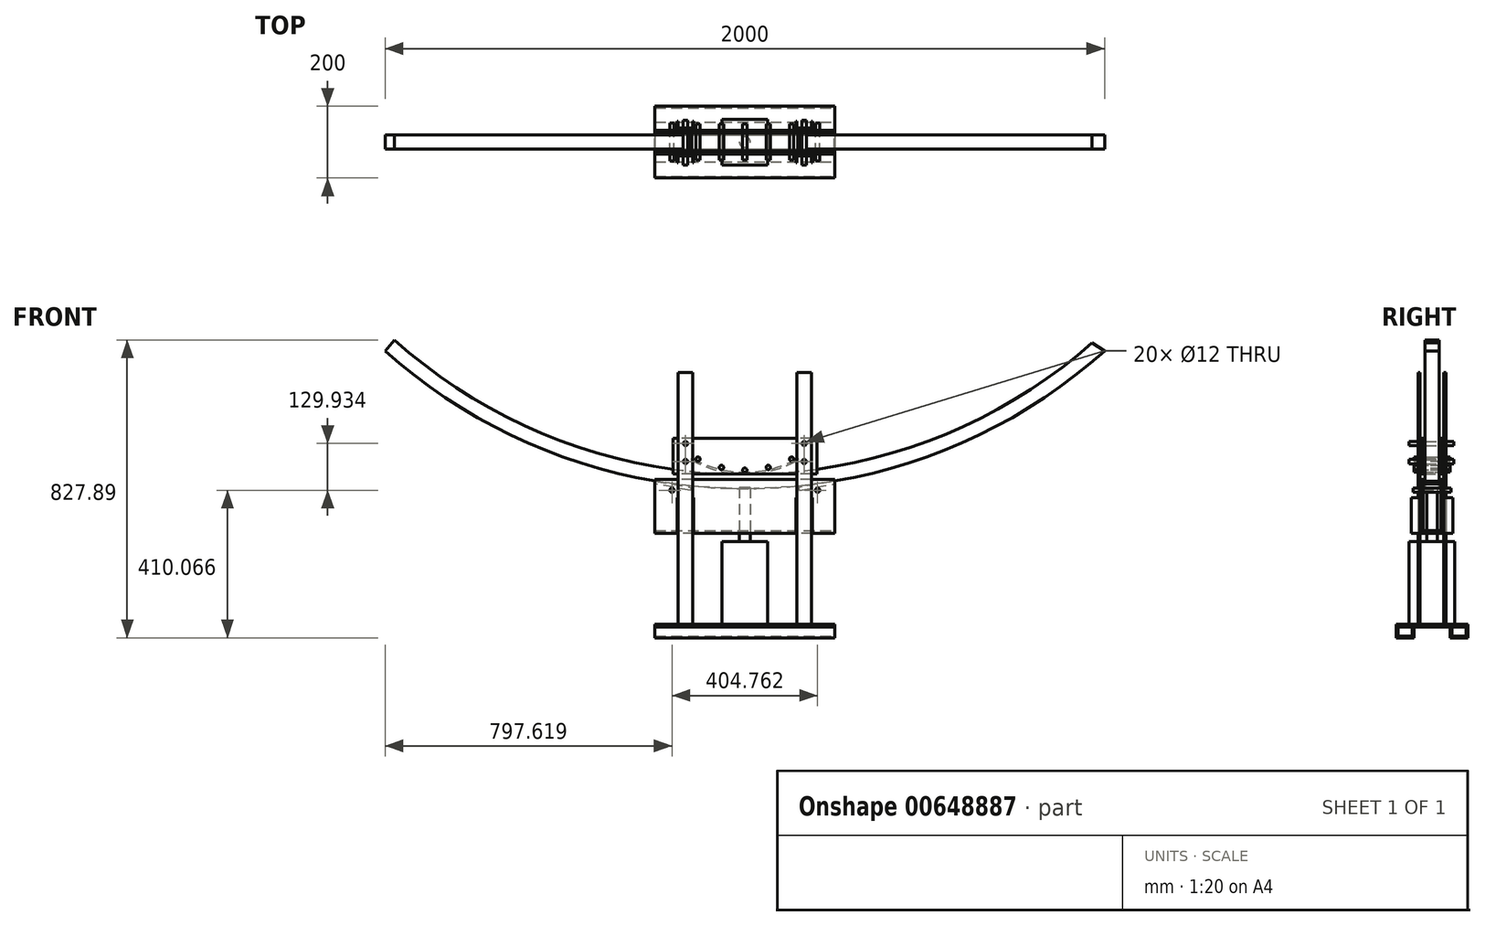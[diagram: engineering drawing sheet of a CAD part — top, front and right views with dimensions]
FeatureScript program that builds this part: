
annotation { "Feature Type Name" : "Feature", "Feature Type Description" : "" }
export const myFeature = defineFeature(function(context is Context, id is Id, definition is map)
    precondition{}
    {
        {
            var Q0;
            Q0=qCreatedBy(makeId("Front.planeOp"),FACE);
            var sketch = newSketch(context, id + "F0", { "sketchPlane" : qUnion([Q0])});
            skArc(sketch, "E0", {"start": v(-1000, 381.97) * mm, "mid": v(0, 0) * mm, "end": v(1000, 381.97) * mm});
            skArc(sketch, "E1", {"start": v(-974.57, 412.89) * mm, "mid": v(-6.16, 40.01) * mm, "end": v(965.36, 404.7) * mm});
            skLineSegment(sketch, "E2", {"start": v(-1000, 381.97) * mm, "end": v(-974.57, 412.89) * mm});
            skLineSegment(sketch, "E3", {"start": v(965.36, 404.7) * mm, "end": v(1000, 381.97) * mm});
            skSolve(sketch);
        }
        {
            var Q0;
            Q0 = qSketchRegion(id + "F0", true);
            extrude(context, id + "F1", {"entities" : qUnion([Q0]), "endBound" : BoundingType.SYMMETRIC, "depth" : 40 * mm, "offsetDistance" : 25 * mm});
        }
        {
            var Q0;
            Q0=qCreatedBy(makeId("Front.planeOp"),FACE);
            var sketch = newSketch(context, id + "F2", { "sketchPlane" : qUnion([Q0])});
            skLineSegment(sketch, "E4", {"start": v(-248.58, 20.64) * mm, "end": v(-150.16, 2.95) * mm});
            skLineSegment(sketch, "E5", {"start": v(-150.16, 2.95) * mm, "end": v(-151.58, -4.92) * mm});
            skLineSegment(sketch, "E6", {"start": v(-151.58, -4.92) * mm, "end": v(-250, 12.77) * mm});
            skLineSegment(sketch, "E7", {"start": v(-250, 12.77) * mm, "end": v(-248.58, 20.64) * mm});
            skLineSegment(sketch, "E8", {"start": v(0, 0) * mm, "end": v(0, 293.06) * mm, "construction": true});
            skLineSegment(sketch, "E9", {"start": v(-364.02, 41.4) * mm, "end": v(0, -24.04) * mm, "construction": true});
            skSolve(sketch);
        }
        {
            var Q0;
            Q0 = qSketchRegion(id + "F2", true);
            extrude(context, id + "F3", {"entities" : qUnion([Q0]), "endBound" : BoundingType.SYMMETRIC, "depth" : 50 * mm, "offsetDistance" : 25 * mm});
        }
        {
            var Q0;
            Q0=makeQuery(id+"F3.opExtrude","SWEPT_BODY",BODY,{"disambiguationData":[OSD([sQuery(id+"F2.wireOp",EDGE,"E4"),sQuery(id+"F2.wireOp",EDGE,"E5"),sQuery(id+"F2.wireOp",EDGE,"E6"),sQuery(id+"F2.wireOp",EDGE,"E7")])]});
            var Q1;
            Q1=makeQuery(id+"F3.opExtrude","SWEPT_BODY",BODY,{"disambiguationData":[OSD([sQuery(id+"F2.wireOp",EDGE,"z8wgNzzR-RekP-I29d-0YfE-zqQQIktSLqPd")])]});
            var Q2;
            Q2=qCreatedBy(makeId("Right.planeOp"),FACE);
            mirror(context, id + "F4", {"entities" : qUnion([Q0, Q1]), "mirrorPlane" : qUnion([Q2])});
        }
        {
            var Q0;
            Q0=qCreatedBy(makeId("Front.planeOp"),FACE);
            var sketch = newSketch(context, id + "F5", { "sketchPlane" : qUnion([Q0])});
            skCircle(sketch, "E10", {"center": v(-202.38, -4.93) * mm, "radius": 6 * mm});
            skLineSegment(sketch, "E11", {"start": v(-200.79, 3.92) * mm, "end": v(-213.25, -65.38) * mm, "construction": true});
            skSolve(sketch);
        }
        {
            var Q0;
            Q0 = qSketchRegion(id + "F5", true);
            extrude(context, id + "F6", {"entities" : qUnion([Q0]), "endBound" : BoundingType.SYMMETRIC, "depth" : (50 + 2 * 8 + 2 * 20) * mm, "offsetDistance" : 25 * mm});
        }
        {
            var Q0;
            Q0=makeQuery(id+"F6.opExtrude","SWEPT_BODY",BODY,{"disambiguationData":[OSD([sQuery(id+"F5.wireOp",EDGE,"E10")])]});
            var Q1;
            Q1=qCreatedBy(makeId("Right.planeOp"),FACE);
            mirror(context, id + "F7", {"entities" : qUnion([Q0]), "mirrorPlane" : qUnion([Q1])});
        }
        {
            var Q0;
            Q0=qCreatedBy(makeId("Front.planeOp"),FACE);
            cPlane(context, id + "F8", {"entities" : qUnion([Q0]), "cplaneType" : CPlaneType.OFFSET, "offset" : 25 * mm, "width" : 150 * mm, "height" : 150 * mm});
        }
        {
            var Q0;
            Q0=qCreatedBy(id+"F8.planeOp",FACE);
            var sketch = newSketch(context, id + "F9", { "sketchPlane" : qUnion([Q0])});
            skLineSegment(sketch, "E12.bottom", {"start": v(250, -125) * mm, "end": v(-250, -125) * mm});
            skLineSegment(sketch, "E12.top", {"start": v(250, 25) * mm, "end": v(-250, 25) * mm});
            skLineSegment(sketch, "E12.left", {"start": v(250, -125) * mm, "end": v(250, 25) * mm});
            skLineSegment(sketch, "E12.right", {"start": v(-250, -125) * mm, "end": v(-250, 25) * mm});
            skPoint(sketch, "E12.middle", {"position": v(0, -50) * mm});
            skSolve(sketch);
        }
        {
            var Q0;
            Q0 = qSketchRegion(id + "F9", true);
            extrude(context, id + "F10", {"entities" : qUnion([Q0]), "depth" : 8 * mm, "offsetDistance" : 25 * mm});
        }
        {
            var Q0;
            Q0=makeQuery(id+"F6.opExtrude","SWEPT_BODY",BODY,{"disambiguationData":[OSD([sQuery(id+"F5.wireOp",EDGE,"E10")])]});
            var Q1;
            Q1=makeQuery(id+"F7.opPattern","COPY",BODY,{"derivedFrom":makeQuery(id+"F6.opExtrude","SWEPT_BODY",BODY,{"disambiguationData":[OSD([sQuery(id+"F5.wireOp",EDGE,"E10")])]}),"instanceName":"1"});
            var Q2;
            Q2=makeQuery(id+"F10.opExtrude","SWEPT_BODY",BODY,{"disambiguationData":[OSD([sQuery(id+"F9.wireOp",EDGE,"E12.bottom"),sQuery(id+"F9.wireOp",EDGE,"E12.top"),sQuery(id+"F9.wireOp",EDGE,"E12.left"),sQuery(id+"F9.wireOp",EDGE,"E12.right")])]});
            booleanBodies(context, id + "F11", {"operationType" : BooleanOperationType.SUBTRACTION, "tools" : qUnion([Q0, Q1]), "targets" : qUnion([Q2]), "keepTools" : true});
        }
        {
            var Q0;
            Q0=makeQuery(id+"F10.opExtrude","SWEPT_BODY",BODY,{"disambiguationData":[OSD([sQuery(id+"F9.wireOp",EDGE,"E12.bottom"),sQuery(id+"F9.wireOp",EDGE,"E12.top"),sQuery(id+"F9.wireOp",EDGE,"E12.left"),sQuery(id+"F9.wireOp",EDGE,"E12.right")])]});
            var Q1;
            Q1=qCreatedBy(makeId("Front.planeOp"),FACE);
            mirror(context, id + "F12", {"entities" : qUnion([Q0]), "mirrorPlane" : qUnion([Q1])});
        }
        {
            var Q0;
            Q0=qCreatedBy(id+"F8.planeOp",FACE);
            var sketch = newSketch(context, id + "F13", { "sketchPlane" : qUnion([Q0])});
            skLineSegment(sketch, "E13.bottom", {"start": v(200, 40) * mm, "end": v(-200, 40) * mm});
            skLineSegment(sketch, "E13.top", {"start": v(200, 140) * mm, "end": v(-200, 140) * mm});
            skLineSegment(sketch, "E13.left", {"start": v(200, 40) * mm, "end": v(200, 140) * mm});
            skLineSegment(sketch, "E13.right", {"start": v(-200, 40) * mm, "end": v(-200, 140) * mm});
            skPoint(sketch, "E13.middle", {"position": v(0, 90) * mm});
            skSolve(sketch);
        }
        {
            var Q0;
            Q0 = qSketchRegion(id + "F13", true);
            extrude(context, id + "F14", {"entities" : qUnion([Q0]), "depth" : 8 * mm, "offsetDistance" : 25 * mm});
        }
        {
            var Q0;
            Q0=makeQuery(id+"F14.opExtrude","SWEPT_BODY",BODY,{"disambiguationData":[OSD([sQuery(id+"F13.wireOp",EDGE,"E13.bottom"),sQuery(id+"F13.wireOp",EDGE,"E13.top"),sQuery(id+"F13.wireOp",EDGE,"E13.left"),sQuery(id+"F13.wireOp",EDGE,"E13.right")])]});
            var Q1;
            Q1=qCreatedBy(makeId("Front.planeOp"),FACE);
            mirror(context, id + "F15", {"entities" : qUnion([Q0]), "mirrorPlane" : qUnion([Q1])});
        }
        {
            var Q0;
            Q0=makeQuery(id+"F12.opPattern","COPY",FACE,{"derivedFrom":makeQuery(id+"F10.opExtrude","SWEPT_FACE",FACE,{"disambiguationData":[OSD([sQuery(id+"F9.wireOp",EDGE,"E12.bottom")])]}),"instanceName":"1"});
            var sketch = newSketch(context, id + "F16", { "sketchPlane" : qUnion([Q0])});
            skLineSegment(sketch, "E14.bottom", {"start": v(-25, 25) * mm, "end": v(250, 25) * mm});
            skLineSegment(sketch, "E14.top", {"start": v(-25, -25) * mm, "end": v(250, -25) * mm});
            skLineSegment(sketch, "E14.right", {"start": v(250, 25) * mm, "end": v(250, -25) * mm});
            skPoint(sketch, "E14.middle", {"position": v(112.5, 0) * mm});
            skLineSegment(sketch, "E15.bottom", {"start": v(-250, 25) * mm, "end": v(25, 25) * mm});
            skLineSegment(sketch, "E15.top", {"start": v(-250, -25) * mm, "end": v(25, -25) * mm});
            skLineSegment(sketch, "E15.left", {"start": v(-250, 25) * mm, "end": v(-250, -25) * mm});
            skPoint(sketch, "E15.middle", {"position": v(-112.5, 0) * mm});
            skSolve(sketch);
        }
        {
            var Q0;
            Q0 = qSketchRegion(id + "F16", true);
            extrude(context, id + "F17", {"entities" : qUnion([Q0]), "oppositeDirection" : true, "depth" : 8 * mm, "offsetDistance" : 25 * mm});
        }
        {
            var Q0;
            Q0=qCreatedBy(makeId("Front.planeOp"),FACE);
            var sketch = newSketch(context, id + "F18", { "sketchPlane" : qUnion([Q0])});
            skArc(sketch, "E16", {"start": v(150, 80.2) * mm, "mid": v(0, 40) * mm, "end": v(-150, 80.2) * mm});
            skLineSegment(sketch, "E17", {"start": v(180.7, 40) * mm, "end": v(-137.19, 40) * mm, "construction": true});
            skArc(sketch, "E18", {"start": v(147.5, 84.52) * mm, "mid": v(0, 45) * mm, "end": v(-147.5, 84.52) * mm});
            skLineSegment(sketch, "E19", {"start": v(150, 80.2) * mm, "end": v(147.5, 84.52) * mm});
            skLineSegment(sketch, "E20", {"start": v(-147.5, 84.52) * mm, "end": v(-150, 80.2) * mm});
            skLineSegment(sketch, "E21", {"start": v(-150, 80.2) * mm, "end": v(-137.46, 72.95) * mm, "construction": true});
            skLineSegment(sketch, "E22", {"start": v(192.57, 104.77) * mm, "end": v(150, 80.2) * mm, "construction": true});
            skSolve(sketch);
        }
        {
            var Q0;
            Q0 = qSketchRegion(id + "F18", true);
            extrude(context, id + "F19", {"entities" : qUnion([Q0]), "endBound" : BoundingType.SYMMETRIC, "depth" : 50 * mm, "offsetDistance" : 25 * mm});
        }
        {
            var Q0;
            Q0=qCreatedBy(makeId("Front.planeOp"),FACE);
            var sketch = newSketch(context, id + "F20", { "sketchPlane" : qUnion([Q0])});
            skCircle(sketch, "E23", {"center": v(0, 51) * mm, "radius": 6 * mm});
            skCircle(sketch, "E24", {"center": v(-65, 58.4) * mm, "radius": 6 * mm});
            skCircle(sketch, "E25", {"center": v(65, 58.4) * mm, "radius": 6 * mm});
            skCircle(sketch, "E26", {"center": v(-130, 81.89) * mm, "radius": 6 * mm});
            skCircle(sketch, "E27", {"center": v(130, 81.89) * mm, "radius": 6 * mm});
            skLineSegment(sketch, "E28", {"start": v(0, 0) * mm, "end": v(0, 155.47) * mm, "construction": true});
            skSolve(sketch);
        }
        {
            var Q0;
            Q0 = qSketchRegion(id + "F20", true);
            extrude(context, id + "F21", {"entities" : qUnion([Q0]), "endBound" : BoundingType.SYMMETRIC, "depth" : 100 * mm, "offsetDistance" : 25 * mm});
        }
        {
            var Q0;
            Q0=qCreatedBy(makeId("Top.planeOp"),FACE);
            cPlane(context, id + "F22", {"entities" : qUnion([Q0]), "cplaneType" : CPlaneType.OFFSET, "offset" : (250 + 127) * mm, "oppositeDirection" : true, "width" : 150 * mm, "height" : 150 * mm});
        }
        {
            var Q0;
            Q0=qCreatedBy(id+"F22.planeOp",FACE);
            var sketch = newSketch(context, id + "F23", { "sketchPlane" : qUnion([Q0])});
            skLineSegment(sketch, "E29.bottom", {"start": v(63.5, 63.5) * mm, "end": v(-63.5, 63.5) * mm});
            skLineSegment(sketch, "E29.top", {"start": v(63.5, -63.5) * mm, "end": v(-63.5, -63.5) * mm});
            skLineSegment(sketch, "E29.left", {"start": v(63.5, 63.5) * mm, "end": v(63.5, -63.5) * mm});
            skLineSegment(sketch, "E29.right", {"start": v(-63.5, 63.5) * mm, "end": v(-63.5, -63.5) * mm});
            skPoint(sketch, "E29.middle", {"position": v(0, 0) * mm});
            skSolve(sketch);
        }
        {
            var Q0;
            Q0 = qSketchRegion(id + "F23", true);
            extrude(context, id + "F24", {"entities" : qUnion([Q0]), "depth" : 230 * mm, "offsetDistance" : 25 * mm});
        }
        {
            var Q0;
            Q0=makeQuery(id+"F24.opExtrude","CAP_FACE",FACE,{"disambiguationData":[OSD([sQuery(id+"F23.wireOp",EDGE,"E29.bottom"),sQuery(id+"F23.wireOp",EDGE,"E29.top"),sQuery(id+"F23.wireOp",EDGE,"E29.left"),sQuery(id+"F23.wireOp",EDGE,"E29.right")])],"isStart":false});
            var sketch = newSketch(context, id + "F25", { "sketchPlane" : qUnion([Q0])});
            skCircle(sketch, "E30", {"center": v(0, 0) * mm, "radius": 15 * mm});
            skSolve(sketch);
        }
        {
            var Q0;
            Q0 = qSketchRegion(id + "F25", true);
            extrude(context, id + "F26", {"entities" : qUnion([Q0]), "depth" : 150 * mm, "offsetDistance" : 25 * mm});
        }
        {
            var Q0;
            Q0=qCreatedBy(id+"F22.planeOp",FACE);
            var sketch = newSketch(context, id + "F27", { "sketchPlane" : qUnion([Q0])});
            skLineSegment(sketch, "E31.bottom", {"start": v(250, 100) * mm, "end": v(-250, 100) * mm});
            skLineSegment(sketch, "E31.top", {"start": v(250, -100) * mm, "end": v(-250, -100) * mm});
            skLineSegment(sketch, "E31.left", {"start": v(250, 100) * mm, "end": v(250, -100) * mm});
            skLineSegment(sketch, "E31.right", {"start": v(-250, 100) * mm, "end": v(-250, -100) * mm});
            skPoint(sketch, "E31.middle", {"position": v(0, 0) * mm});
            skSolve(sketch);
        }
        {
            var Q0;
            Q0 = qSketchRegion(id + "F27", true);
            extrude(context, id + "F28", {"entities" : qUnion([Q0]), "oppositeDirection" : true, "depth" : 8 * mm, "offsetDistance" : 25 * mm});
        }
        {
            var Q0;
            Q0=makeQuery(id+"F28.opExtrude","CAP_FACE",FACE,{"disambiguationData":[OSD([sQuery(id+"F27.wireOp",EDGE,"E31.bottom"),sQuery(id+"F27.wireOp",EDGE,"E31.top"),sQuery(id+"F27.wireOp",EDGE,"E31.left"),sQuery(id+"F27.wireOp",EDGE,"E31.right")])],"isStart":true});
            var sketch = newSketch(context, id + "F29", { "sketchPlane" : qUnion([Q0])});
            skLineSegment(sketch, "E32.bottom", {"start": v(-185, 39) * mm, "end": v(-145, 39) * mm});
            skLineSegment(sketch, "E32.top", {"start": v(-185, 33) * mm, "end": v(-145, 33) * mm});
            skLineSegment(sketch, "E32.left", {"start": v(-185, 39) * mm, "end": v(-185, 33) * mm});
            skLineSegment(sketch, "E32.right", {"start": v(-145, 39) * mm, "end": v(-145, 33) * mm});
            skLineSegment(sketch, "E33.bottom", {"start": v(-185, -33) * mm, "end": v(-145, -33) * mm});
            skLineSegment(sketch, "E33.top", {"start": v(-185, -39) * mm, "end": v(-145, -39) * mm});
            skLineSegment(sketch, "E33.left", {"start": v(-185, -33) * mm, "end": v(-185, -39) * mm});
            skLineSegment(sketch, "E33.right", {"start": v(-145, -33) * mm, "end": v(-145, -39) * mm});
            skLineSegment(sketch, "E34.bottom", {"start": v(145, -33) * mm, "end": v(185, -33) * mm});
            skLineSegment(sketch, "E34.top", {"start": v(145, -39) * mm, "end": v(185, -39) * mm});
            skLineSegment(sketch, "E34.left", {"start": v(145, -33) * mm, "end": v(145, -39) * mm});
            skLineSegment(sketch, "E34.right", {"start": v(185, -33) * mm, "end": v(185, -39) * mm});
            skLineSegment(sketch, "E35.bottom", {"start": v(145, 39) * mm, "end": v(185, 39) * mm});
            skLineSegment(sketch, "E35.top", {"start": v(145, 33) * mm, "end": v(185, 33) * mm});
            skLineSegment(sketch, "E35.left", {"start": v(145, 39) * mm, "end": v(145, 33) * mm});
            skLineSegment(sketch, "E35.right", {"start": v(185, 39) * mm, "end": v(185, 33) * mm});
            skSolve(sketch);
        }
        {
            var Q0;
            Q0 = qSketchRegion(id + "F29", true);
            extrude(context, id + "F30", {"entities" : qUnion([Q0]), "depth" : 700 * mm, "offsetDistance" : 25 * mm});
        }
        {
            var Q0;
            Q0=makeQuery(id+"F30.opExtrude","SWEPT_FACE",FACE,{"disambiguationData":[OSD([sQuery(id+"F29.wireOp",EDGE,"E33.top")])]});
            var sketch = newSketch(context, id + "F31", { "sketchPlane" : qUnion([Q0])});
            skCircle(sketch, "E36", {"center": v(-165, 125) * mm, "radius": 6 * mm});
            skCircle(sketch, "E37", {"center": v(-165, 75) * mm, "radius": 6 * mm});
            skCircle(sketch, "E38", {"center": v(165, 125) * mm, "radius": 6 * mm});
            skCircle(sketch, "E39", {"center": v(165, 75) * mm, "radius": 6 * mm});
            skLineSegment(sketch, "E40", {"start": v(-165, 125) * mm, "end": v(-165, 75) * mm, "construction": true});
            skLineSegment(sketch, "E41", {"start": v(165, 125) * mm, "end": v(165, 75) * mm, "construction": true});
            skSolve(sketch);
        }
        {
            var Q0;
            Q0 = qSketchRegion(id + "F31", true);
            extrude(context, id + "F32", {"entities" : qUnion([Q0]), "depth" : 25 * mm, "offsetDistance" : 25 * mm, "hasSecondDirection" : true, "secondDirectionOppositeDirection" : true, "secondDirectionDepth" : 100 * mm});
        }
        {
            var Q0;
            Q0=makeQuery(id+"F32.opExtrude","SWEPT_BODY",BODY,{"disambiguationData":[OSD([sQuery(id+"F31.wireOp",EDGE,"E37")])]});
            var Q1;
            Q1=makeQuery(id+"F32.opExtrude","SWEPT_BODY",BODY,{"disambiguationData":[OSD([sQuery(id+"F31.wireOp",EDGE,"E39")])]});
            var Q2;
            Q2=makeQuery(id+"F32.opExtrude","SWEPT_BODY",BODY,{"disambiguationData":[OSD([sQuery(id+"F31.wireOp",EDGE,"E38")])]});
            var Q3;
            Q3=makeQuery(id+"F32.opExtrude","SWEPT_BODY",BODY,{"disambiguationData":[OSD([sQuery(id+"F31.wireOp",EDGE,"E36")])]});
            var Q4;
            Q4=makeQuery(id+"F30.opExtrude","SWEPT_BODY",BODY,{"disambiguationData":[OSD([sQuery(id+"F29.wireOp",EDGE,"E33.bottom"),sQuery(id+"F29.wireOp",EDGE,"E33.top"),sQuery(id+"F29.wireOp",EDGE,"E33.left"),sQuery(id+"F29.wireOp",EDGE,"E33.right")])]});
            var Q5;
            Q5=makeQuery(id+"F30.opExtrude","SWEPT_BODY",BODY,{"disambiguationData":[OSD([sQuery(id+"F29.wireOp",EDGE,"E32.bottom"),sQuery(id+"F29.wireOp",EDGE,"E32.top"),sQuery(id+"F29.wireOp",EDGE,"E32.left"),sQuery(id+"F29.wireOp",EDGE,"E32.right")])]});
            var Q6;
            Q6=makeQuery(id+"F14.opExtrude","SWEPT_BODY",BODY,{"disambiguationData":[OSD([sQuery(id+"F13.wireOp",EDGE,"E13.bottom"),sQuery(id+"F13.wireOp",EDGE,"E13.top"),sQuery(id+"F13.wireOp",EDGE,"E13.left"),sQuery(id+"F13.wireOp",EDGE,"E13.right")])]});
            var Q7;
            Q7=makeQuery(id+"F15.opPattern","COPY",BODY,{"derivedFrom":makeQuery(id+"F14.opExtrude","SWEPT_BODY",BODY,{"disambiguationData":[OSD([sQuery(id+"F13.wireOp",EDGE,"E13.bottom"),sQuery(id+"F13.wireOp",EDGE,"E13.top"),sQuery(id+"F13.wireOp",EDGE,"E13.left"),sQuery(id+"F13.wireOp",EDGE,"E13.right")])]}),"instanceName":"1"});
            var Q8;
            Q8=makeQuery(id+"F30.opExtrude","SWEPT_BODY",BODY,{"disambiguationData":[OSD([sQuery(id+"F29.wireOp",EDGE,"E35.bottom"),sQuery(id+"F29.wireOp",EDGE,"E35.top"),sQuery(id+"F29.wireOp",EDGE,"E35.left"),sQuery(id+"F29.wireOp",EDGE,"E35.right")])]});
            var Q9;
            Q9=makeQuery(id+"F30.opExtrude","SWEPT_BODY",BODY,{"disambiguationData":[OSD([sQuery(id+"F29.wireOp",EDGE,"E34.bottom"),sQuery(id+"F29.wireOp",EDGE,"E34.top"),sQuery(id+"F29.wireOp",EDGE,"E34.left"),sQuery(id+"F29.wireOp",EDGE,"E34.right")])]});
            booleanBodies(context, id + "F33", {"operationType" : BooleanOperationType.SUBTRACTION, "tools" : qUnion([Q0, Q1, Q2, Q3]), "targets" : qUnion([Q4, Q5, Q6, Q7, Q8, Q9]), "keepTools" : true});
        }
        {
            var Q0;
            Q0=makeQuery(id+"F10.opExtrude","SWEPT_FACE",FACE,{"disambiguationData":[OSD([sQuery(id+"F9.wireOp",EDGE,"E12.bottom")])]});
            var sketch = newSketch(context, id + "F34", { "sketchPlane" : qUnion([Q0])});
            skLineSegment(sketch, "E42.bottom", {"start": v(-185, 33) * mm, "end": v(-188, 33) * mm});
            skLineSegment(sketch, "E42.top", {"start": v(-185, 58) * mm, "end": v(-188, 58) * mm});
            skLineSegment(sketch, "E42.left", {"start": v(-185, 33) * mm, "end": v(-185, 58) * mm});
            skLineSegment(sketch, "E42.right", {"start": v(-188, 33) * mm, "end": v(-188, 58) * mm});
            skLineSegment(sketch, "E43.bottom", {"start": v(-145, 58) * mm, "end": v(-142, 58) * mm});
            skLineSegment(sketch, "E43.top", {"start": v(-145, 33) * mm, "end": v(-142, 33) * mm});
            skLineSegment(sketch, "E43.left", {"start": v(-145, 58) * mm, "end": v(-145, 33) * mm});
            skLineSegment(sketch, "E43.right", {"start": v(-142, 58) * mm, "end": v(-142, 33) * mm});
            skSolve(sketch);
        }
        {
            var Q0;
            Q0 = qSketchRegion(id + "F34", true);
            extrude(context, id + "F35", {"entities" : qUnion([Q0]), "oppositeDirection" : true, "depth" : 100 * mm, "offsetDistance" : 25 * mm});
        }
        {
            var Q0;
            Q0=makeQuery(id+"F35.opExtrude","SWEPT_BODY",BODY,{"disambiguationData":[OSD([sQuery(id+"F34.wireOp",EDGE,"E42.bottom"),sQuery(id+"F34.wireOp",EDGE,"E42.top"),sQuery(id+"F34.wireOp",EDGE,"E42.left"),sQuery(id+"F34.wireOp",EDGE,"E42.right")])]});
            var Q1;
            Q1=makeQuery(id+"F35.opExtrude","SWEPT_BODY",BODY,{"disambiguationData":[OSD([sQuery(id+"F34.wireOp",EDGE,"E43.bottom"),sQuery(id+"F34.wireOp",EDGE,"E43.top"),sQuery(id+"F34.wireOp",EDGE,"E43.left"),sQuery(id+"F34.wireOp",EDGE,"E43.right")])]});
            var Q2;
            Q2=qCreatedBy(makeId("Right.planeOp"),FACE);
            mirror(context, id + "F36", {"entities" : qUnion([Q0, Q1]), "mirrorPlane" : qUnion([Q2])});
        }
        {
            var Q0;
            Q0=makeQuery(id+"F35.opExtrude","SWEPT_BODY",BODY,{"disambiguationData":[OSD([sQuery(id+"F34.wireOp",EDGE,"E42.bottom"),sQuery(id+"F34.wireOp",EDGE,"E42.top"),sQuery(id+"F34.wireOp",EDGE,"E42.left"),sQuery(id+"F34.wireOp",EDGE,"E42.right")])]});
            var Q1;
            Q1=makeQuery(id+"F35.opExtrude","SWEPT_BODY",BODY,{"disambiguationData":[OSD([sQuery(id+"F34.wireOp",EDGE,"E43.bottom"),sQuery(id+"F34.wireOp",EDGE,"E43.top"),sQuery(id+"F34.wireOp",EDGE,"E43.left"),sQuery(id+"F34.wireOp",EDGE,"E43.right")])]});
            var Q2;
            Q2=makeQuery(id+"F36.opPattern","COPY",BODY,{"derivedFrom":makeQuery(id+"F35.opExtrude","SWEPT_BODY",BODY,{"disambiguationData":[OSD([sQuery(id+"F34.wireOp",EDGE,"E43.bottom"),sQuery(id+"F34.wireOp",EDGE,"E43.top"),sQuery(id+"F34.wireOp",EDGE,"E43.left"),sQuery(id+"F34.wireOp",EDGE,"E43.right")])]}),"instanceName":"1"});
            var Q3;
            Q3=makeQuery(id+"F36.opPattern","COPY",BODY,{"derivedFrom":makeQuery(id+"F35.opExtrude","SWEPT_BODY",BODY,{"disambiguationData":[OSD([sQuery(id+"F34.wireOp",EDGE,"E42.bottom"),sQuery(id+"F34.wireOp",EDGE,"E42.top"),sQuery(id+"F34.wireOp",EDGE,"E42.left"),sQuery(id+"F34.wireOp",EDGE,"E42.right")])]}),"instanceName":"1"});
            var Q4;
            Q4=qCreatedBy(makeId("Front.planeOp"),FACE);
            mirror(context, id + "F37", {"entities" : qUnion([Q0, Q1, Q2, Q3]), "mirrorPlane" : qUnion([Q4])});
        }
        {
            var Q0;
            Q0=makeQuery(id+"F28.opExtrude","SWEPT_FACE",FACE,{"disambiguationData":[OSD([sQuery(id+"F27.wireOp",EDGE,"E31.left")])]});
            var sketch = newSketch(context, id + "F38", { "sketchPlane" : qUnion([Q0])});
            skLineSegment(sketch, "E44.bottom", {"start": v(-100, -385) * mm, "end": v(-95, -385) * mm});
            skLineSegment(sketch, "E44.top", {"start": v(-100, -415) * mm, "end": v(-50, -415) * mm});
            skLineSegment(sketch, "E44.left", {"start": v(-100, -385) * mm, "end": v(-100, -415) * mm});
            skLineSegment(sketch, "E44.right", {"start": v(-50, -385) * mm, "end": v(-50, -415) * mm});
            skLineSegment(sketch, "E45.top", {"start": v(-95, -410) * mm, "end": v(-55, -410) * mm});
            skLineSegment(sketch, "E45.left", {"start": v(-95, -385) * mm, "end": v(-95, -410) * mm});
            skLineSegment(sketch, "E45.right", {"start": v(-55, -385) * mm, "end": v(-55, -410) * mm});
            skLineSegment(sketch, "E46.trimOffspring", {"start": v(-55, -385) * mm, "end": v(-50, -385) * mm});
            skSolve(sketch);
        }
        {
            var Q0;
            Q0 = qSketchRegion(id + "F38", true);
            var Q1;
            Q1=makeQuery(id+"F28.opExtrude","SWEPT_FACE",FACE,{"disambiguationData":[OSD([sQuery(id+"F27.wireOp",EDGE,"E31.right")])]});
            extrude(context, id + "F39", {"entities" : qUnion([Q0]), "endBound" : BoundingType.UP_TO_SURFACE, "oppositeDirection" : true, "depth" : 25 * mm, "endBoundEntityFace" : qUnion([Q1]), "offsetDistance" : 25 * mm});
        }
        {
            var Q0;
            Q0=makeQuery(id+"F39.opExtrude","SWEPT_BODY",BODY,{"disambiguationData":[OSD([sQuery(id+"F38.wireOp",EDGE,"E44.bottom"),sQuery(id+"F38.wireOp",EDGE,"E44.top"),sQuery(id+"F38.wireOp",EDGE,"E44.left"),sQuery(id+"F38.wireOp",EDGE,"E44.right"),sQuery(id+"F38.wireOp",EDGE,"E45.top"),sQuery(id+"F38.wireOp",EDGE,"E45.left"),sQuery(id+"F38.wireOp",EDGE,"E45.right"),sQuery(id+"F38.wireOp",EDGE,"E46.trimOffspring")])]});
            var Q1;
            Q1=qCreatedBy(makeId("Front.planeOp"),FACE);
            mirror(context, id + "F40", {"entities" : qUnion([Q0]), "mirrorPlane" : qUnion([Q1])});
        }
    });
